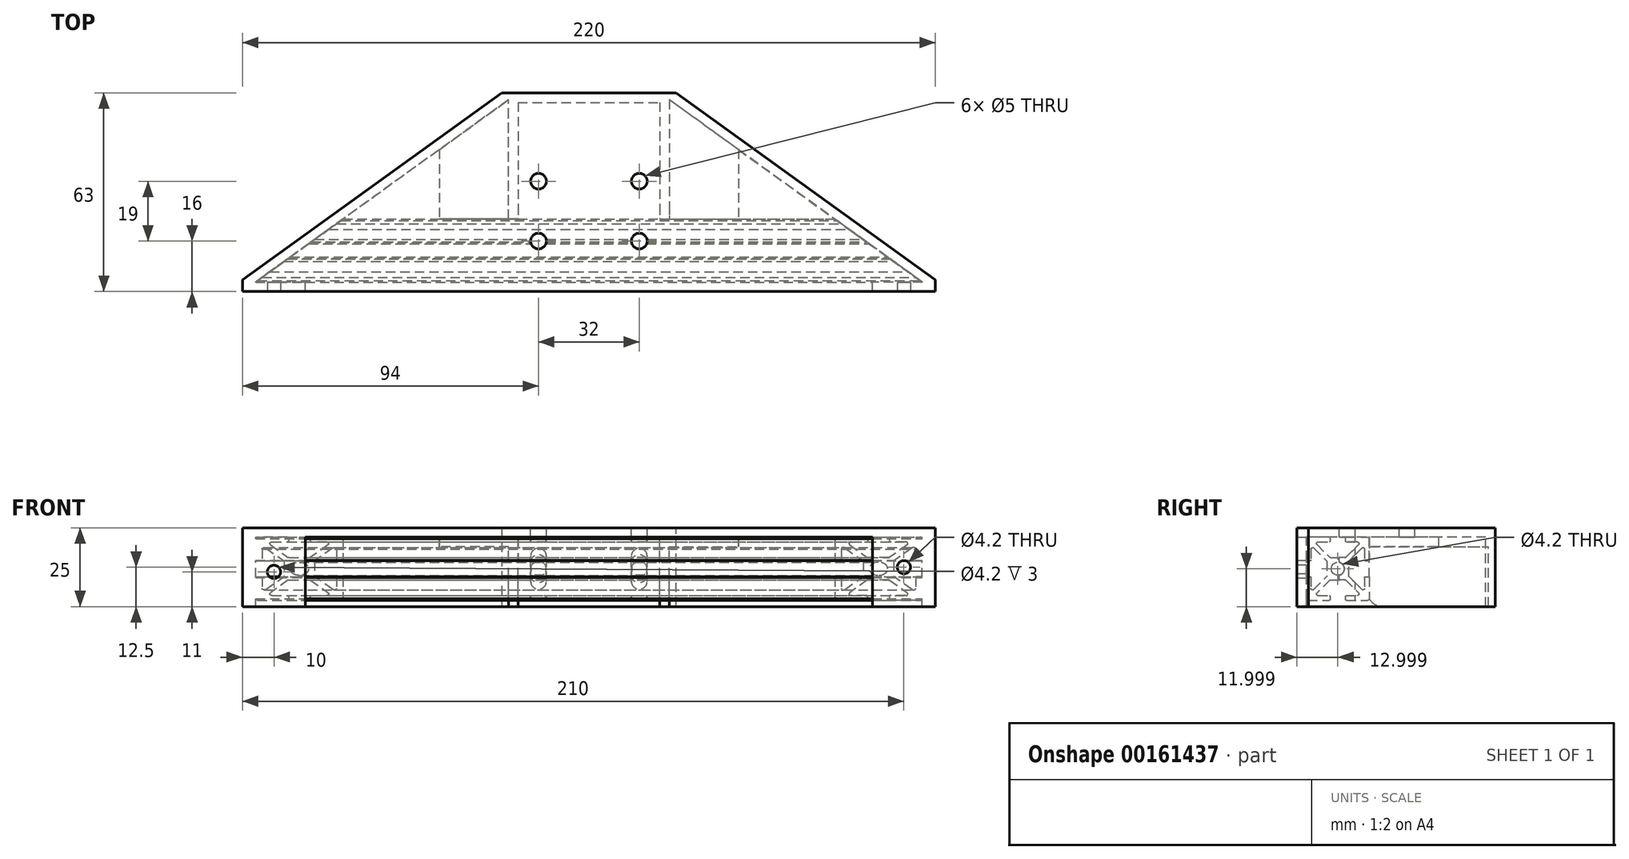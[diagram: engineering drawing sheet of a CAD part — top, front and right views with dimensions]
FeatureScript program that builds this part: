
annotation { "Feature Type Name" : "Feature", "Feature Type Description" : "" }
export const myFeature = defineFeature(function(context is Context, id is Id, definition is map)
    precondition{}
    {
        {
            var Q0;
            Q0=qCreatedBy(makeId("Top.planeOp"),FACE);
            var sketch = newSketch(context, id + "F0", { "sketchPlane" : qUnion([Q0])});
            skLineSegment(sketch, "E0", {"start": v(-110, 0) * mm, "end": v(110, 0) * mm});
            skLineSegment(sketch, "E1.bottom", {"start": v(-38.97, 0) * mm, "end": v(38.97, 0) * mm});
            skLineSegment(sketch, "E1.top", {"start": v(-22.5, 63) * mm, "end": v(22.5, 63) * mm});
            skLineSegment(sketch, "E2", {"start": v(-22.5, 63) * mm, "end": v(-110, 0) * mm});
            skLineSegment(sketch, "E3", {"start": v(22.5, 63) * mm, "end": v(110, 0) * mm});
            skLineSegment(sketch, "E4", {"start": v(0, 0) * mm, "end": v(0, 18.37) * mm});
            skSolve(sketch);
        }
        {
            var Q0;
            Q0 = qSketchRegion(id + "F0", true);
            extrude(context, id + "F1", {"entities" : qUnion([Q0]), "oppositeDirection" : true, "depth" : 3 * mm});
        }
        {
            var Q0;
            Q0=makeQuery(id+"F1.opExtrude","CAP_FACE",FACE,{"disambiguationData":[OSD([sQuery(id+"F0.wireOp",EDGE,"E0"),sQuery(id+"F0.wireOp",EDGE,"E1.bottom"),sQuery(id+"F0.wireOp",EDGE,"E1.top"),sQuery(id+"F0.wireOp",EDGE,"E2"),sQuery(id+"F0.wireOp",EDGE,"E3")])],"isStart":false});
            var sketch = newSketch(context, id + "F2", { "sketchPlane" : qUnion([Q0])});
            skLineSegment(sketch, "E5", {"start": v(-22.5, -60) * mm, "end": v(22.5, -60) * mm});
            skLineSegment(sketch, "E6", {"start": v(-22.5, -63) * mm, "end": v(22.5, -63) * mm});
            skLineSegment(sketch, "E7", {"start": v(-22.5, -63) * mm, "end": v(-22.5, -60) * mm});
            skLineSegment(sketch, "E8", {"start": v(22.5, -63) * mm, "end": v(22.5, -60) * mm});
            skLineSegment(sketch, "E9", {"start": v(-110, 0) * mm, "end": v(110, 0) * mm});
            skLineSegment(sketch, "E10", {"start": v(110, 0) * mm, "end": v(105.83, -3) * mm});
            skLineSegment(sketch, "E11", {"start": v(105.83, -3) * mm, "end": v(90, -3) * mm});
            skLineSegment(sketch, "E12", {"start": v(-105.83, -3) * mm, "end": v(-110, 0) * mm});
            skLineSegment(sketch, "E13", {"start": v(-90, 0) * mm, "end": v(-90, -3) * mm});
            skLineSegment(sketch, "E14", {"start": v(90, 0) * mm, "end": v(90, -3) * mm});
            skLineSegment(sketch, "E15.trimOffspring", {"start": v(-90, -3) * mm, "end": v(-105.83, -3) * mm});
            skSolve(sketch);
        }
        {
            var Q0;
            {var subQ0=sQuery(id+"F2.wireOp",EDGE,"E12");Q0=makeQuery(id+"F2.imprint","IMPRINT",FACE,{"disambiguationData":[TD([[makeQuery(id+"F2.imprint","IMPRINT",EDGE,{"derivedFrom":subQ0}),-1.0]])]});}
            var Q1;
            {var subQ0=sQuery(id+"F2.wireOp",EDGE,"E10");Q1=makeQuery(id+"F2.imprint","IMPRINT",FACE,{"disambiguationData":[TD([[makeQuery(id+"F2.imprint","IMPRINT",EDGE,{"derivedFrom":subQ0}),1.0]])]});}
            var Q2;
            Q2=makeQuery(id+"F2.imprint","IMPRINT",FACE,{"disambiguationData":[TD([[makeQuery(id+"F2.imprint","IMPRINT",EDGE,{"derivedFrom":sQuery(id+"F2.wireOp",EDGE,"E5")}),-1.0]])]});
            extrude(context, id + "F3", {"entities" : qUnion([Q0, Q1, Q2]), "operationType" : NewBodyOperationType.ADD, "depth" : 22 * mm});
        }
        {
            var Q0;
            {var subQ0=sQuery(id+"F2.wireOp",EDGE,"E9");Q0=makeQuery(id+"F3.boolean.opBoolean","MERGE",FACE,{"derivedFrom":[makeQuery(id+"F1.opExtrude","SWEPT_FACE",FACE,{"disambiguationData":[OSD([sQuery(id+"F0.wireOp",EDGE,"E0"),sQuery(id+"F0.wireOp",EDGE,"E1.bottom")])]}),makeQuery(id+"F3.opExtrude","SWEPT_FACE",FACE,{"disambiguationData":[OSD([subQ0]),TDD([makeQuery(id+"F2.imprint","IMPRINT",EDGE,{"disambiguationData":[TD([[makeQuery(id+"F2.imprint","INTERSECT",VERTEX,{"derivedFrom":[subQ0,sQuery(id+"F2.wireOp",EDGE,"E12")]}),-1.0]])],"derivedFrom":subQ0})])]}),makeQuery(id+"F3.opExtrude","SWEPT_FACE",FACE,{"disambiguationData":[OSD([subQ0]),TDD([makeQuery(id+"F2.imprint","IMPRINT",EDGE,{"disambiguationData":[TD([[makeQuery(id+"F2.imprint","INTERSECT",VERTEX,{"derivedFrom":[subQ0,sQuery(id+"F2.wireOp",EDGE,"E10")]}),1.0]])],"derivedFrom":subQ0})])]})]});}
            var sketch = newSketch(context, id + "F4", { "sketchPlane" : qUnion([Q0])});
            skCircle(sketch, "E16", {"center": v(-100, -14) * mm, "radius": 2.1 * mm});
            skPoint(sketch, "E16.centerSnap0", {"position": v(-90, -14) * mm});
            skPoint(sketch, "E16.centerSnap1", {"position": v(-100, -25) * mm});
            skCircle(sketch, "E17", {"center": v(100, -12.5) * mm, "radius": 2.1 * mm});
            skPoint(sketch, "E17.centerSnap0", {"position": v(110, -12.5) * mm});
            skPoint(sketch, "E17.centerSnap1", {"position": v(100, -25) * mm});
            skSolve(sketch);
        }
        {
            var Q0;
            Q0 = qSketchRegion(id + "F4", true);
            extrude(context, id + "F5", {"entities" : qUnion([Q0]), "operationType" : NewBodyOperationType.REMOVE, "oppositeDirection" : true, "depth" : 3 * mm});
        }
        {
            var Q0;
            Q0=makeQuery(id+"F1.opExtrude","CAP_FACE",FACE,{"disambiguationData":[OSD([sQuery(id+"F0.wireOp",EDGE,"E0"),sQuery(id+"F0.wireOp",EDGE,"E1.bottom"),sQuery(id+"F0.wireOp",EDGE,"E1.top"),sQuery(id+"F0.wireOp",EDGE,"E2"),sQuery(id+"F0.wireOp",EDGE,"E3")])],"isStart":false});
            var sketch = newSketch(context, id + "F6", { "sketchPlane" : qUnion([Q0])});
            skLineSegment(sketch, "E18.bottom", {"start": v(105.83, -3) * mm, "end": v(-105.83, -3) * mm});
            skLineSegment(sketch, "E18.top", {"start": v(105.83, -23) * mm, "end": v(-105.83, -23) * mm});
            skLineSegment(sketch, "E18.left", {"start": v(105.83, -3) * mm, "end": v(105.83, -23) * mm});
            skLineSegment(sketch, "E18.right", {"start": v(-105.83, -3) * mm, "end": v(-105.83, -23) * mm});
            skLineSegment(sketch, "E19", {"start": v(-78.06, -23) * mm, "end": v(-105.83, -3) * mm});
            skLineSegment(sketch, "E20", {"start": v(105.83, -3) * mm, "end": v(78.06, -23) * mm});
            skSolve(sketch);
        }
        {
            var Q0;
            Q0 = qSketchRegion(id + "F6", true);
            extrude(context, id + "F7", {"entities" : qUnion([Q0]), "operationType" : NewBodyOperationType.ADD, "depth" : 20 * mm});
        }
        {
            var Q0;
            Q0=makeQuery(id+"F7.opExtrude","SWEPT_FACE",FACE,{"disambiguationData":[OSD([sQuery(id+"F6.wireOp",EDGE,"E18.left")])]});
            var sketch = newSketch(context, id + "F8", { "sketchPlane" : qUnion([Q0])});
            skLineSegment(sketch, "E21.top", {"start": v(3, -23) * mm, "end": v(3, -23) * mm});
            skLineSegment(sketch, "E21.right", {"start": v(23, -3) * mm, "end": v(23, -3) * mm});
            skLineSegment(sketch, "E22.bottom", {"start": v(10.25, -3) * mm, "end": v(3.5, -3) * mm});
            skLineSegment(sketch, "E22.top", {"start": v(22.5, -23) * mm, "end": v(15.76, -23) * mm});
            skLineSegment(sketch, "E22.left", {"start": v(23, -3.5) * mm, "end": v(23, -10.25) * mm});
            skLineSegment(sketch, "E22.right", {"start": v(3, -15.75) * mm, "end": v(3, -22.5) * mm});
            skCircle(sketch, "E23", {"center": v(13, -13) * mm, "radius": 2.1 * mm});
            skLineSegment(sketch, "E24.left", {"start": v(10.5, -3.25) * mm, "end": v(10.5, -4.25) * mm});
            skLineSegment(sketch, "E24.right", {"start": v(15.5, -3.25) * mm, "end": v(15.5, -4.25) * mm});
            skLineSegment(sketch, "E25", {"start": v(9.5, -10.67) * mm, "end": v(9.5, -15.34) * mm});
            skLineSegment(sketch, "E26", {"start": v(16.5, -10.67) * mm, "end": v(16.5, -15.34) * mm});
            skLineSegment(sketch, "E27", {"start": v(6.77, -21.5) * mm, "end": v(10.25, -21.5) * mm});
            skLineSegment(sketch, "E28", {"start": v(4.5, -15.75) * mm, "end": v(4.5, -19.23) * mm});
            skLineSegment(sketch, "E29", {"start": v(21.5, -6.77) * mm, "end": v(21.5, -10.25) * mm});
            skLineSegment(sketch, "E30", {"start": v(6.77, -4.5) * mm, "end": v(10.25, -4.5) * mm});
            skLineSegment(sketch, "E31.bottom", {"start": v(21.75, -10.5) * mm, "end": v(22.75, -10.5) * mm});
            skLineSegment(sketch, "E31.top", {"start": v(3.25, -15.5) * mm, "end": v(4.25, -15.5) * mm});
            skPoint(sketch, "E31.middle", {"position": v(23, -13) * mm});
            skLineSegment(sketch, "E32", {"start": v(6.41, -5.35) * mm, "end": v(10.49, -9.43) * mm});
            skLineSegment(sketch, "E33", {"start": v(15.51, -16.57) * mm, "end": v(19.58, -20.65) * mm});
            skLineSegment(sketch, "E34", {"start": v(19.58, -5.35) * mm, "end": v(15.51, -9.43) * mm});
            skLineSegment(sketch, "E35", {"start": v(10.49, -16.57) * mm, "end": v(6.41, -20.65) * mm});
            skArc(sketch, "E36.filletArc", {"start": v(6.77, -4.5) * mm, "mid": v(6.3, -4.8) * mm, "end": v(6.41, -5.35) * mm});
            skPoint(sketch, "E37.newPointB", {"position": v(23, -4.5) * mm});
            skArc(sketch, "E37.filletArc", {"start": v(19.58, -5.35) * mm, "mid": v(19.7, -4.8) * mm, "end": v(19.23, -4.5) * mm});
            skArc(sketch, "E38.filletArc", {"start": v(21.5, -6.77) * mm, "mid": v(21.2, -6.3) * mm, "end": v(20.65, -6.42) * mm});
            skArc(sketch, "E39.filletArc", {"start": v(20.65, -19.59) * mm, "mid": v(21.2, -19.7) * mm, "end": v(21.5, -19.23) * mm});
            skArc(sketch, "E40.filletArc", {"start": v(19.23, -21.5) * mm, "mid": v(19.7, -21.2) * mm, "end": v(19.58, -20.65) * mm});
            skArc(sketch, "E41.filletArc", {"start": v(6.41, -20.65) * mm, "mid": v(6.3, -21.2) * mm, "end": v(6.77, -21.5) * mm});
            skArc(sketch, "E42.filletArc", {"start": v(4.5, -19.23) * mm, "mid": v(4.8, -19.7) * mm, "end": v(5.35, -19.59) * mm});
            skArc(sketch, "E43.filletArc", {"start": v(5.35, -6.42) * mm, "mid": v(4.78, -6.32) * mm, "end": v(4.5, -6.82) * mm});
            skPoint(sketch, "E44.visualSharp", {"position": v(3, -3) * mm});
            skArc(sketch, "E44.filletArc", {"start": v(3.5, -3) * mm, "mid": v(3.15, -3.15) * mm, "end": v(3, -3.5) * mm});
            skPoint(sketch, "E45.visualSharp", {"position": v(23, -3) * mm});
            skArc(sketch, "E45.filletArc", {"start": v(23, -3.5) * mm, "mid": v(22.85, -3.15) * mm, "end": v(22.5, -3) * mm});
            skPoint(sketch, "E46.visualSharp", {"position": v(23, -23) * mm});
            skArc(sketch, "E46.filletArc", {"start": v(22.5, -23) * mm, "mid": v(22.85, -22.85) * mm, "end": v(23, -22.5) * mm});
            skPoint(sketch, "E47.visualSharp", {"position": v(3, -23) * mm});
            skArc(sketch, "E47.filletArc", {"start": v(3, -22.5) * mm, "mid": v(3.15, -22.85) * mm, "end": v(3.5, -23) * mm});
            skArc(sketch, "E48.filletArc", {"start": v(10.25, -4.5) * mm, "mid": v(10.43, -4.43) * mm, "end": v(10.5, -4.25) * mm});
            skArc(sketch, "E49.filletArc", {"start": v(4.5, -15.75) * mm, "mid": v(4.43, -15.57) * mm, "end": v(4.25, -15.5) * mm});
            skArc(sketch, "E50.filletArc", {"start": v(10.5, -3.25) * mm, "mid": v(10.43, -3.07) * mm, "end": v(10.25, -3) * mm});
            skLineSegment(sketch, "E51", {"start": v(15.75, -3) * mm, "end": v(22.5, -3) * mm});
            skLineSegment(sketch, "E52", {"start": v(19.23, -4.5) * mm, "end": v(15.75, -4.5) * mm});
            skLineSegment(sketch, "E53", {"start": v(4.5, -6.82) * mm, "end": v(4.5, -10.25) * mm});
            skLineSegment(sketch, "E54", {"start": v(21.75, -15.5) * mm, "end": v(22.75, -15.5) * mm});
            skPoint(sketch, "E55.visualSharp", {"position": v(15.5, -4.5) * mm});
            skArc(sketch, "E55.filletArc", {"start": v(15.5, -4.25) * mm, "mid": v(15.57, -4.43) * mm, "end": v(15.75, -4.5) * mm});
            skPoint(sketch, "E56.visualSharp", {"position": v(15.5, -3) * mm});
            skArc(sketch, "E56.filletArc", {"start": v(15.75, -3) * mm, "mid": v(15.57, -3.07) * mm, "end": v(15.5, -3.25) * mm});
            skPoint(sketch, "E57.newPointB", {"position": v(3, -10.5) * mm});
            skArc(sketch, "E57.filletArc", {"start": v(21.5, -10.25) * mm, "mid": v(21.57, -10.43) * mm, "end": v(21.75, -10.5) * mm});
            skLineSegment(sketch, "E58", {"start": v(21.5, -15.75) * mm, "end": v(21.5, -19.23) * mm});
            skPoint(sketch, "E59.visualSharp", {"position": v(21.5, -15.5) * mm});
            skArc(sketch, "E59.filletArc", {"start": v(21.75, -15.5) * mm, "mid": v(21.57, -15.57) * mm, "end": v(21.5, -15.75) * mm});
            skArc(sketch, "E60.filletArc", {"start": v(22.75, -10.5) * mm, "mid": v(22.93, -10.43) * mm, "end": v(23, -10.25) * mm});
            skLineSegment(sketch, "E61", {"start": v(23, -15.75) * mm, "end": v(23, -22.5) * mm});
            skPoint(sketch, "E62.visualSharp", {"position": v(23, -15.5) * mm});
            skArc(sketch, "E62.filletArc", {"start": v(23, -15.75) * mm, "mid": v(22.93, -15.57) * mm, "end": v(22.75, -15.5) * mm});
            skLineSegment(sketch, "E63", {"start": v(4.25, -10.5) * mm, "end": v(3.25, -10.5) * mm});
            skPoint(sketch, "E64.visualSharp", {"position": v(4.5, -10.5) * mm});
            skArc(sketch, "E64.filletArc", {"start": v(4.25, -10.5) * mm, "mid": v(4.43, -10.43) * mm, "end": v(4.5, -10.25) * mm});
            skPoint(sketch, "E65.newPointA", {"position": v(3, -15.5) * mm});
            skArc(sketch, "E65.filletArc", {"start": v(3.25, -15.5) * mm, "mid": v(3.07, -15.57) * mm, "end": v(3, -15.75) * mm});
            skLineSegment(sketch, "E66", {"start": v(3, -10.25) * mm, "end": v(3, -3.5) * mm});
            skArc(sketch, "E67.filletArc", {"start": v(3, -10.25) * mm, "mid": v(3.07, -10.43) * mm, "end": v(3.25, -10.5) * mm});
            skPoint(sketch, "E68.newPointB", {"position": v(10.5, -10.5) * mm});
            skLineSegment(sketch, "E69", {"start": v(20.65, -19.59) * mm, "end": v(16.57, -15.51) * mm});
            skPoint(sketch, "E69.endSnap0", {"position": v(16.5, -13.75) * mm});
            skPoint(sketch, "E70.newPointA", {"position": v(16.5, -15.44) * mm});
            skPoint(sketch, "E70.newPointB", {"position": v(16.5, -23) * mm});
            skArc(sketch, "E70.filletArc", {"start": v(16.5, -15.34) * mm, "mid": v(16.52, -15.43) * mm, "end": v(16.57, -15.51) * mm});
            skLineSegment(sketch, "E71", {"start": v(10.66, -16.5) * mm, "end": v(15.33, -16.5) * mm});
            skArc(sketch, "E72.filletArc", {"start": v(15.51, -16.57) * mm, "mid": v(15.43, -16.52) * mm, "end": v(15.33, -16.5) * mm});
            skArc(sketch, "E73.filletArc", {"start": v(10.66, -16.5) * mm, "mid": v(10.57, -16.52) * mm, "end": v(10.49, -16.57) * mm});
            skLineSegment(sketch, "E74", {"start": v(5.35, -19.59) * mm, "end": v(9.43, -15.51) * mm});
            skLineSegment(sketch, "E75", {"start": v(5.35, -6.42) * mm, "end": v(9.43, -10.49) * mm});
            skArc(sketch, "E76.filletArc", {"start": v(9.5, -10.67) * mm, "mid": v(9.48, -10.57) * mm, "end": v(9.43, -10.49) * mm});
            skArc(sketch, "E77.filletArc", {"start": v(9.43, -15.51) * mm, "mid": v(9.48, -15.43) * mm, "end": v(9.5, -15.34) * mm});
            skLineSegment(sketch, "E78", {"start": v(20.65, -6.42) * mm, "end": v(16.57, -10.49) * mm});
            skPoint(sketch, "E79.newPointB", {"position": v(16.5, -4.5) * mm});
            skArc(sketch, "E79.filletArc", {"start": v(16.57, -10.49) * mm, "mid": v(16.52, -10.57) * mm, "end": v(16.5, -10.67) * mm});
            skLineSegment(sketch, "E80", {"start": v(10.66, -9.5) * mm, "end": v(15.33, -9.5) * mm});
            skArc(sketch, "E81.filletArc", {"start": v(10.49, -9.43) * mm, "mid": v(10.57, -9.48) * mm, "end": v(10.66, -9.5) * mm});
            skArc(sketch, "E82.filletArc", {"start": v(15.33, -9.5) * mm, "mid": v(15.43, -9.48) * mm, "end": v(15.51, -9.43) * mm});
            skPoint(sketch, "E83.orphan", {"position": v(10.5, -3) * mm});
            skPoint(sketch, "E84.orphan", {"position": v(13, -3) * mm});
            skPoint(sketch, "E85.orphan", {"position": v(3, -13) * mm});
            skPoint(sketch, "E86.trimOffspring.end.orphan", {"position": v(13, -23) * mm});
            skLineSegment(sketch, "E87", {"start": v(15.51, -3.75) * mm, "end": v(15.51, -4.33) * mm});
            skPoint(sketch, "E87.startSnap0", {"position": v(15.5, -3.75) * mm});
            skLineSegment(sketch, "E88", {"start": v(10.5, -3.75) * mm, "end": v(10.5, -4.25) * mm});
            skPoint(sketch, "E89.start.orphan", {"position": v(10.66, -21.5) * mm});
            skLineSegment(sketch, "E90.trimOffspring", {"start": v(15.76, -21.5) * mm, "end": v(19.23, -21.5) * mm});
            skLineSegment(sketch, "E91.trimOffspring", {"start": v(10.25, -23) * mm, "end": v(3.5, -23) * mm});
            skLineSegment(sketch, "E92.trimOffspring", {"start": v(15.51, -21.75) * mm, "end": v(15.51, -22.75) * mm});
            skLineSegment(sketch, "E93.trimOffspring", {"start": v(10.5, -21.75) * mm, "end": v(10.5, -22.75) * mm});
            skArc(sketch, "E94.filletArc", {"start": v(10.5, -21.75) * mm, "mid": v(10.43, -21.57) * mm, "end": v(10.25, -21.5) * mm});
            skPoint(sketch, "E95.visualSharp", {"position": v(15.51, -21.5) * mm});
            skArc(sketch, "E95.filletArc", {"start": v(15.76, -21.5) * mm, "mid": v(15.58, -21.57) * mm, "end": v(15.51, -21.75) * mm});
            skPoint(sketch, "E96.visualSharp", {"position": v(10.5, -23) * mm});
            skArc(sketch, "E96.filletArc", {"start": v(10.25, -23) * mm, "mid": v(10.43, -22.93) * mm, "end": v(10.5, -22.75) * mm});
            skPoint(sketch, "E97.visualSharp", {"position": v(15.51, -23) * mm});
            skArc(sketch, "E97.filletArc", {"start": v(15.51, -22.75) * mm, "mid": v(15.58, -22.93) * mm, "end": v(15.76, -23) * mm});
            skLineSegment(sketch, "E98.trimOffspring", {"start": v(23, -15.7) * mm, "end": v(23, -22.56) * mm});
            skLineSegment(sketch, "E99.trimOffspring", {"start": v(15.75, -23) * mm, "end": v(22.52, -23) * mm});
            skLineSegment(sketch, "E100", {"start": v(3, -22.5) * mm, "end": v(3, -15.75) * mm});
            skLineSegment(sketch, "E101", {"start": v(3, -3.5) * mm, "end": v(3, -10.25) * mm});
            skLineSegment(sketch, "E102.trimOffspring", {"start": v(23, -3.44) * mm, "end": v(23, -10.3) * mm});
            skLineSegment(sketch, "E103.trimOffspring", {"start": v(23, -23) * mm, "end": v(23, -23) * mm});
            skLineSegment(sketch, "E104.trimOffspring", {"start": v(3.48, -23) * mm, "end": v(10.26, -23) * mm});
            skSolve(sketch);
        }
        {
            var Q0;
            Q0=makeQuery(id+"F8.imprint","IMPRINT",FACE,{"disambiguationData":[TD([[makeQuery(id+"F8.imprint","IMPRINT",EDGE,{"derivedFrom":sQuery(id+"F8.wireOp",EDGE,"E25")}),-1.0]])]});
            var Q1;
            Q1=makeQuery(id+"F8.imprint","IMPRINT",FACE,{"disambiguationData":[TD([[makeQuery(id+"F8.imprint","IMPRINT",EDGE,{"derivedFrom":sQuery(id+"F8.wireOp",EDGE,"E24.left")}),1.0]])]});
            var Q2;
            Q2=makeQuery(id+"F8.imprint","IMPRINT",FACE,{"disambiguationData":[TD([[makeQuery(id+"F8.imprint","IMPRINT",EDGE,{"derivedFrom":sQuery(id+"F8.wireOp",EDGE,"E27")}),1.0]])]});
            var Q3;
            {var subQ0=sQuery(id+"F8.wireOp",EDGE,"E47.filletArc");var subQ1=sQuery(id+"F6.wireOp",EDGE,"E18.left");var subQ4=makeQuery(id+"F7.opExtrude","CAP_EDGE",EDGE,{"disambiguationData":[OSD([subQ1])],"isStart":false});var subQ5=makeQuery(id+"F8.imprint","INTERSECT",VERTEX,{"derivedFrom":[subQ4,subQ0]});Q3=makeQuery(id+"F8.imprint","IMPRINT",FACE,{"disambiguationData":[TD([[makeQuery(id+"F8.imprint","IMPRINT",EDGE,{"disambiguationData":[TD([[subQ5,1.0]])],"derivedFrom":subQ0}),-1.0]])]});}
            var Q4;
            Q4=makeQuery(id+"F8.imprint","IMPRINT",FACE,{"disambiguationData":[TD([[makeQuery(id+"F8.imprint","IMPRINT",EDGE,{"derivedFrom":sQuery(id+"F8.wireOp",EDGE,"E23")}),1.0]])]});
            extrude(context, id + "F9", {"entities" : qUnion([Q0, Q1, Q2, Q3, Q4]), "operationType" : NewBodyOperationType.REMOVE, "oppositeDirection" : true, "depth" : 220 * mm});
        }
        {
            var Q0;
            {var subQ0=sQuery(id+"F6.wireOp",EDGE,"E18.left");var subQ2=sQuery(id+"F0.wireOp",EDGE,"E1.top");var subQ6=sQuery(id+"F0.wireOp",EDGE,"E2");var subQ7=sQuery(id+"F0.wireOp",EDGE,"E3");var subQ8=sQuery(id+"F0.wireOp",EDGE,"E1.bottom");var subQ9=sQuery(id+"F0.wireOp",EDGE,"E0");var subQ10=makeQuery(id+"F1.opExtrude","CAP_FACE",FACE,{"disambiguationData":[OSD([subQ9,subQ8,subQ2,subQ6,subQ7])],"isStart":false});var subQ13=sQuery(id+"F2.wireOp",EDGE,"E13");Q0=makeQuery(id+"F9.boolean.opBoolean","MERGE",FACE,{"derivedFrom":[makeQuery(id+"F7.boolean.opBoolean","SPLIT",FACE,{"disambiguationData":[TD([makeQuery(id+"F3.opExtrude","SWEPT_FACE",FACE,{"disambiguationData":[OSD([subQ13])]})])],"derivedFrom":subQ10}),makeQuery(id+"F7.boolean.opBoolean","SPLIT",FACE,{"disambiguationData":[TD([makeQuery(id+"F1.opExtrude","SWEPT_FACE",FACE,{"disambiguationData":[OSD([subQ2])]})])],"derivedFrom":subQ10}),makeQuery(id+"F9.opExtrude","SWEPT_FACE",FACE,{"disambiguationData":[OSD([subQ0]),TDD([makeQuery(id+"F8.imprint","IMPRINT",EDGE,{"derivedFrom":makeQuery(id+"F7.opExtrude","CAP_EDGE",EDGE,{"disambiguationData":[OSD([subQ0])],"isStart":true})})])]})]});}
            var sketch = newSketch(context, id + "F10", { "sketchPlane" : qUnion([Q0])});
            skLineSegment(sketch, "E105.bottom", {"start": v(-22.5, -63) * mm, "end": v(-47.5, -63) * mm});
            skLineSegment(sketch, "E105.top", {"start": v(-22.5, -23) * mm, "end": v(-47.5, -23) * mm});
            skLineSegment(sketch, "E105.left", {"start": v(-22.5, -63) * mm, "end": v(-22.5, -23) * mm});
            skLineSegment(sketch, "E105.right", {"start": v(-47.5, -63) * mm, "end": v(-47.5, -23) * mm});
            skLineSegment(sketch, "E106.bottom", {"start": v(22.5, -63) * mm, "end": v(47.5, -63) * mm});
            skLineSegment(sketch, "E106.top", {"start": v(22.5, -23) * mm, "end": v(47.5, -23) * mm});
            skLineSegment(sketch, "E106.left", {"start": v(22.5, -63) * mm, "end": v(22.5, -23) * mm});
            skLineSegment(sketch, "E106.right", {"start": v(47.5, -63) * mm, "end": v(47.5, -23) * mm});
            skSolve(sketch);
        }
        {
            var Q0;
            Q0 = qSketchRegion(id + "F10", true);
            extrude(context, id + "F11", {"entities" : qUnion([Q0]), "operationType" : NewBodyOperationType.ADD, "depth" : 3 * mm});
        }
        {
            var Q0;
            Q0=makeQuery(id+"F11.opExtrude","CAP_FACE",FACE,{"disambiguationData":[OSD([sQuery(id+"F10.wireOp",EDGE,"E106.bottom"),sQuery(id+"F10.wireOp",EDGE,"E106.top"),sQuery(id+"F10.wireOp",EDGE,"E106.left"),sQuery(id+"F10.wireOp",EDGE,"E106.right")])],"isStart":false});
            var sketch = newSketch(context, id + "F12", { "sketchPlane" : qUnion([Q0])});
            skLineSegment(sketch, "E107.bottom", {"start": v(22.5, -63) * mm, "end": v(25.5, -63) * mm});
            skLineSegment(sketch, "E107.top", {"start": v(22.5, -23) * mm, "end": v(25.5, -23) * mm});
            skLineSegment(sketch, "E107.left", {"start": v(22.5, -63) * mm, "end": v(22.5, -23) * mm});
            skLineSegment(sketch, "E107.right", {"start": v(25.5, -63) * mm, "end": v(25.5, -23) * mm});
            skSolve(sketch);
        }
        {
            var Q0;
            Q0=makeQuery(id+"F11.opExtrude","CAP_FACE",FACE,{"disambiguationData":[OSD([sQuery(id+"F10.wireOp",EDGE,"E105.bottom"),sQuery(id+"F10.wireOp",EDGE,"E105.top"),sQuery(id+"F10.wireOp",EDGE,"E105.left"),sQuery(id+"F10.wireOp",EDGE,"E105.right")])],"isStart":false});
            var sketch = newSketch(context, id + "F13", { "sketchPlane" : qUnion([Q0])});
            skLineSegment(sketch, "E108.bottom", {"start": v(-22.5, -23) * mm, "end": v(-25.5, -23) * mm});
            skLineSegment(sketch, "E108.top", {"start": v(-22.5, -63) * mm, "end": v(-25.5, -63) * mm});
            skLineSegment(sketch, "E108.left", {"start": v(-22.5, -23) * mm, "end": v(-22.5, -63) * mm});
            skLineSegment(sketch, "E108.right", {"start": v(-25.5, -23) * mm, "end": v(-25.5, -63) * mm});
            skSolve(sketch);
        }
        {
            var Q0;
            {var subQ1=sQuery(id+"F13.wireOp",EDGE,"E108.bottom");Q0=makeQuery(id+"F13.imprint","IMPRINT",FACE,{"disambiguationData":[TD([[makeQuery(id+"F13.imprint","IMPRINT",EDGE,{"derivedFrom":subQ1}),1.0]])]});}
            var Q1;
            {var subQ3=sQuery(id+"F12.wireOp",EDGE,"E107.bottom");Q1=makeQuery(id+"F12.imprint","IMPRINT",FACE,{"disambiguationData":[TD([[makeQuery(id+"F12.imprint","IMPRINT",EDGE,{"derivedFrom":subQ3}),1.0]])]});}
            extrude(context, id + "F14", {"entities" : qUnion([Q0, Q1]), "operationType" : NewBodyOperationType.ADD, "depth" : 19 * mm});
        }
        {
            var Q0;
            Q0=makeQuery(id+"F14.opExtrude","CAP_EDGE",EDGE,{"disambiguationData":[OSD([sQuery(id+"F13.wireOp",EDGE,"E108.bottom")])],"isStart":false});
            var Q1;
            Q1=makeQuery(id+"F14.opExtrude","CAP_EDGE",EDGE,{"disambiguationData":[OSD([sQuery(id+"F12.wireOp",EDGE,"E107.top")])],"isStart":false});
            fillet(context, id + "F15", {"entities" : qUnion([Q0, Q1]), "radius" : 5 * mm, "tangentPropagation" : true, "allowEdgeOverflow" : false});
        }
        {
            var Q0;
            {var subQ0=sQuery(id+"F6.wireOp",EDGE,"E18.left");var subQ1=sQuery(id+"F10.wireOp",EDGE,"E105.right");Q0=makeQuery(id+"F11.boolean.opBoolean","SPLIT",EDGE,{"disambiguationData":[topologyDisambiguationEdgeConnected([makeQuery(id+"F9.opExtrude","SWEPT_FACE",FACE,{"disambiguationData":[OSD([subQ0]),TDD([makeQuery(id+"F8.imprint","IMPRINT",EDGE,{"derivedFrom":makeQuery(id+"F7.opExtrude","CAP_EDGE",EDGE,{"disambiguationData":[OSD([subQ0])],"isStart":true})})])]})])],"derivedFrom":makeQuery(id+"F11.opExtrude","CAP_EDGE",EDGE,{"disambiguationData":[OSD([subQ1])],"isStart":true})});}
            var Q1;
            {var subQ0=sQuery(id+"F6.wireOp",EDGE,"E18.left");var subQ1=sQuery(id+"F10.wireOp",EDGE,"E106.right");Q1=makeQuery(id+"F11.boolean.opBoolean","SPLIT",EDGE,{"disambiguationData":[topologyDisambiguationEdgeConnected([makeQuery(id+"F9.opExtrude","SWEPT_FACE",FACE,{"disambiguationData":[OSD([subQ0]),TDD([makeQuery(id+"F8.imprint","IMPRINT",EDGE,{"derivedFrom":makeQuery(id+"F7.opExtrude","CAP_EDGE",EDGE,{"disambiguationData":[OSD([subQ0])],"isStart":true})})])]})])],"derivedFrom":makeQuery(id+"F11.opExtrude","CAP_EDGE",EDGE,{"disambiguationData":[OSD([subQ1])],"isStart":true})});}
            var Q2;
            Q2=makeQuery(id+"F11.opExtrude","CAP_EDGE",EDGE,{"disambiguationData":[OSD([sQuery(id+"F10.wireOp",EDGE,"E106.left")])],"isStart":true});
            var Q3;
            Q3=makeQuery(id+"F11.opExtrude","CAP_EDGE",EDGE,{"disambiguationData":[OSD([sQuery(id+"F10.wireOp",EDGE,"E105.left")])],"isStart":true});
            var Q4;
            Q4=makeQuery(id+"F3.opExtrude","CAP_EDGE",EDGE,{"disambiguationData":[OSD([sQuery(id+"F2.wireOp",EDGE,"E5")])],"isStart":true});
            fillet(context, id + "F16", {"entities" : qUnion([Q0, Q1, Q2, Q3, Q4]), "radius" : 1 * mm, "tangentPropagation" : true, "allowEdgeOverflow" : false});
        }
        {
            var Q0;
            Q0=makeQuery(id+"F1.opExtrude","CAP_FACE",FACE,{"disambiguationData":[OSD([sQuery(id+"F0.wireOp",EDGE,"E0"),sQuery(id+"F0.wireOp",EDGE,"E1.bottom"),sQuery(id+"F0.wireOp",EDGE,"E1.top"),sQuery(id+"F0.wireOp",EDGE,"E2"),sQuery(id+"F0.wireOp",EDGE,"E3")])],"isStart":true});
            var sketch = newSketch(context, id + "F17", { "sketchPlane" : qUnion([Q0])});
            skLineSegment(sketch, "E109", {"start": v(-22.5, 63) * mm, "end": v(-110, 0) * mm});
            skLineSegment(sketch, "E110", {"start": v(-110, 0) * mm, "end": v(-110, 65.26) * mm});
            skLineSegment(sketch, "E111", {"start": v(-110, 65.26) * mm, "end": v(-22.5, 63) * mm});
            skLineSegment(sketch, "E112", {"start": v(22.5, 63) * mm, "end": v(110, 63) * mm});
            skLineSegment(sketch, "E113", {"start": v(110, 63) * mm, "end": v(110, 0) * mm});
            skSolve(sketch);
        }
        {
            var Q0;
            Q0=makeQuery(id+"F17.imprint","IMPRINT",FACE,{"disambiguationData":[TD([[makeQuery(id+"F17.imprint","IMPRINT",EDGE,{"derivedFrom":sQuery(id+"F17.wireOp",EDGE,"E109")}),-1.0]])]});
            var Q1;
            Q1=makeQuery(id+"F17.imprint","IMPRINT",FACE,{"disambiguationData":[TD([[makeQuery(id+"F17.imprint","IMPRINT",EDGE,{"derivedFrom":sQuery(id+"F17.wireOp",EDGE,"E112")}),-1.0]])]});
            extrude(context, id + "F18", {"entities" : qUnion([Q0, Q1]), "operationType" : NewBodyOperationType.REMOVE, "oppositeDirection" : true, "depth" : 25 * mm});
        }
        {
            var Q0;
            Q0=makeQuery(id+"F1.opExtrude","CAP_FACE",FACE,{"disambiguationData":[OSD([sQuery(id+"F0.wireOp",EDGE,"E0"),sQuery(id+"F0.wireOp",EDGE,"E1.bottom"),sQuery(id+"F0.wireOp",EDGE,"E1.top"),sQuery(id+"F0.wireOp",EDGE,"E2"),sQuery(id+"F0.wireOp",EDGE,"E3")])],"isStart":true});
            var sketch = newSketch(context, id + "F19", { "sketchPlane" : qUnion([Q0])});
            skCircle(sketch, "E114", {"center": v(-16, 35) * mm, "radius": 2.5 * mm});
            skCircle(sketch, "E115", {"center": v(16, 35) * mm, "radius": 2.5 * mm});
            skPoint(sketch, "E116.endSnap0", {"position": v(16, 17.5) * mm});
            skCircle(sketch, "E117", {"center": v(-16, 16) * mm, "radius": 2.5 * mm});
            skCircle(sketch, "E118", {"center": v(16, 16) * mm, "radius": 2.5 * mm});
            skSolve(sketch);
        }
        {
            var Q0;
            Q0=makeQuery(id+"F19.imprint","IMPRINT",FACE,{"disambiguationData":[TD([[makeQuery(id+"F19.imprint","IMPRINT",EDGE,{"derivedFrom":sQuery(id+"F19.wireOp",EDGE,"E115")}),1.0]])]});
            var Q1;
            Q1=makeQuery(id+"F19.imprint","IMPRINT",FACE,{"disambiguationData":[TD([[makeQuery(id+"F19.imprint","IMPRINT",EDGE,{"derivedFrom":sQuery(id+"F19.wireOp",EDGE,"E117")}),1.0]])]});
            var Q2;
            Q2=makeQuery(id+"F19.imprint","IMPRINT",FACE,{"disambiguationData":[TD([[makeQuery(id+"F19.imprint","IMPRINT",EDGE,{"derivedFrom":sQuery(id+"F19.wireOp",EDGE,"E118")}),1.0]])]});
            var Q3;
            Q3=makeQuery(id+"F19.imprint","IMPRINT",FACE,{"disambiguationData":[TD([[makeQuery(id+"F19.imprint","IMPRINT",EDGE,{"derivedFrom":sQuery(id+"F19.wireOp",EDGE,"E114")}),1.0]])]});
            extrude(context, id + "F20", {"entities" : qUnion([Q0, Q1, Q2, Q3]), "operationType" : NewBodyOperationType.REMOVE, "oppositeDirection" : true, "depth" : 23 * mm});
        }
        {
            var Q0;
            {var subQ0=sQuery(id+"F0.wireOp",EDGE,"E3");Q0=makeQuery(id+"F18.boolean.opBoolean","MERGE",FACE,{"derivedFrom":[makeQuery(id+"F3.boolean.opBoolean","MERGE",FACE,{"derivedFrom":[makeQuery(id+"F1.opExtrude","SWEPT_FACE",FACE,{"disambiguationData":[OSD([subQ0])]}),makeQuery(id+"F3.opExtrude","SWEPT_FACE",FACE,{"disambiguationData":[OSD([sQuery(id+"F2.wireOp",EDGE,"E10")])]})]}),makeQuery(id+"F18.opExtrude","SWEPT_FACE",FACE,{"disambiguationData":[OSD([subQ0])]})]});}
            var sketch = newSketch(context, id + "F21", { "sketchPlane" : qUnion([Q0])});
            skLineSegment(sketch, "E119.bottom", {"start": v(-89.27, 0) * mm, "end": v(18.55, 0) * mm});
            skLineSegment(sketch, "E119.top", {"start": v(-89.27, -25) * mm, "end": v(18.55, -25) * mm});
            skLineSegment(sketch, "E119.left", {"start": v(-89.27, 0) * mm, "end": v(-89.27, -25) * mm});
            skLineSegment(sketch, "E119.right", {"start": v(18.55, 0) * mm, "end": v(18.55, -25) * mm});
            skSolve(sketch);
        }
        {
            var Q0;
            Q0 = qSketchRegion(id + "F21", true);
            extrude(context, id + "F22", {"entities" : qUnion([Q0]), "operationType" : NewBodyOperationType.ADD, "depth" : 3 * mm});
        }
        {
            var Q0;
            Q0=makeQuery(id+"F18.boolean.opBoolean","MERGE",FACE,{"derivedFrom":[makeQuery(id+"F3.boolean.opBoolean","MERGE",FACE,{"derivedFrom":[makeQuery(id+"F1.opExtrude","SWEPT_FACE",FACE,{"disambiguationData":[OSD([sQuery(id+"F0.wireOp",EDGE,"E2")])]}),makeQuery(id+"F3.opExtrude","SWEPT_FACE",FACE,{"disambiguationData":[OSD([sQuery(id+"F2.wireOp",EDGE,"E12")])]})]}),makeQuery(id+"F18.opExtrude","SWEPT_FACE",FACE,{"disambiguationData":[OSD([sQuery(id+"F17.wireOp",EDGE,"E109")])]})]});
            var sketch = newSketch(context, id + "F23", { "sketchPlane" : qUnion([Q0])});
            skLineSegment(sketch, "E120.bottom", {"start": v(-18.55, 0) * mm, "end": v(89.27, 0) * mm});
            skLineSegment(sketch, "E120.top", {"start": v(-18.55, -25) * mm, "end": v(89.27, -25) * mm});
            skLineSegment(sketch, "E120.left", {"start": v(-18.55, 0) * mm, "end": v(-18.55, -25) * mm});
            skLineSegment(sketch, "E120.right", {"start": v(89.27, 0) * mm, "end": v(89.27, -25) * mm});
            skSolve(sketch);
        }
        {
            var Q0;
            Q0 = qSketchRegion(id + "F23", true);
            extrude(context, id + "F24", {"entities" : qUnion([Q0]), "operationType" : NewBodyOperationType.ADD, "depth" : 3 * mm});
        }
        {
            var Q0;
            Q0=makeQuery(id+"F24.boolean.opBoolean","MERGE",FACE,{"derivedFrom":[makeQuery(id+"F22.boolean.opBoolean","MERGE",FACE,{"derivedFrom":[makeQuery(id+"F1.opExtrude","CAP_FACE",FACE,{"disambiguationData":[OSD([sQuery(id+"F0.wireOp",EDGE,"E0"),sQuery(id+"F0.wireOp",EDGE,"E1.bottom"),sQuery(id+"F0.wireOp",EDGE,"E1.top"),sQuery(id+"F0.wireOp",EDGE,"E2"),sQuery(id+"F0.wireOp",EDGE,"E3")])],"isStart":true}),makeQuery(id+"F22.opExtrude","SWEPT_FACE",FACE,{"disambiguationData":[OSD([sQuery(id+"F21.wireOp",EDGE,"E119.bottom")])]})]}),makeQuery(id+"F24.opExtrude","SWEPT_FACE",FACE,{"disambiguationData":[OSD([sQuery(id+"F23.wireOp",EDGE,"E120.bottom")])]})]});
            var sketch = newSketch(context, id + "F25", { "sketchPlane" : qUnion([Q0])});
            skLineSegment(sketch, "E121.bottom", {"start": v(27.63, 63) * mm, "end": v(-29.82, 63) * mm});
            skLineSegment(sketch, "E121.top", {"start": v(27.63, 68.18) * mm, "end": v(-29.82, 68.18) * mm});
            skLineSegment(sketch, "E121.left", {"start": v(27.63, 63) * mm, "end": v(27.63, 68.18) * mm});
            skLineSegment(sketch, "E121.right", {"start": v(-29.82, 63) * mm, "end": v(-29.82, 68.18) * mm});
            skLineSegment(sketch, "E122.bottom", {"start": v(-122.24, 12.25) * mm, "end": v(-110, 12.25) * mm});
            skLineSegment(sketch, "E122.top", {"start": v(-122.24, 0) * mm, "end": v(-110, 0) * mm});
            skLineSegment(sketch, "E122.left", {"start": v(-122.24, 12.25) * mm, "end": v(-122.24, 0) * mm});
            skLineSegment(sketch, "E122.right", {"start": v(-110, 12.25) * mm, "end": v(-110, 0) * mm});
            skLineSegment(sketch, "E123.bottom", {"start": v(110, 0) * mm, "end": v(114.6, 0) * mm});
            skLineSegment(sketch, "E123.top", {"start": v(110, 7.03) * mm, "end": v(114.6, 7.03) * mm});
            skLineSegment(sketch, "E123.left", {"start": v(110, 0) * mm, "end": v(110, 7.03) * mm});
            skLineSegment(sketch, "E123.right", {"start": v(114.6, 0) * mm, "end": v(114.6, 7.03) * mm});
            skSolve(sketch);
        }
        {
            var Q0;
            Q0 = qSketchRegion(id + "F25", true);
            extrude(context, id + "F26", {"entities" : qUnion([Q0]), "operationType" : NewBodyOperationType.REMOVE, "oppositeDirection" : true, "depth" : 25 * mm});
        }
    });
